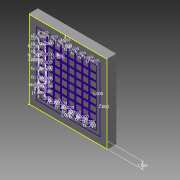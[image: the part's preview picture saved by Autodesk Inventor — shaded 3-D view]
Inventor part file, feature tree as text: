
AUTODESK INVENTOR PART (.ipt)
format: ipt  version: 2015 (Build 190159000, 159)  size: 167,424 bytes
history: native  units: in
note: dims shown in document units (in); Inventor stores cm internally (conversion verified against a paired STEP export)
features: fillet x4, sketch x3, extrude x1
ambient origin geometry x8: Origin, YZ Plane, XZ Plane, XY Plane, X Axis, Y Axis, Z Axis, Center Point
bodies: Solid1 (feature_tree)
feature tree (8):
  extrude  "Extrusion1"  Depth=22.0in
  fillet  "Fillet1"  Radius=2.5in
  fillet  "Fillet2"  Radius=0.125in
  fillet  "Fillet3"  Radius=0.125in
  fillet  "Fillet4"  Radius=0.125in
  sketch  "Sketch2"  dims[d7=0.125in]
  sketch  "Sketch3"  dims[d12=1.9688in d13=1.9688in d14=1.9688in d15=1.9688in d16=1.9688in d17=1.9688in d18=1.9688in d19=1.9688in d20=1.9688in d21=1.9688in d22=1.9688in d23=1.9688in d24=1.9688in d25=1.9688in d26=1.9688in d27=1.9688in d28=1.0in d29=1.0in d30=1.0in d31=1.0in d32=2.0in d33=2.0in d34=2.0in d35=2.0in d36=0.2in d37=0.2in d38=0.2in d39=0.2in d40=0.2in d41=0.2in d42=0.2in d43=0.2in d44=0.2in d45=0.2in d46=0.2in d47=0.2in d48=0.2in d49=0.2in d50=0.2in d51=0.2in d52=0.2in d53=0.2in d54=0.2in d55=0.2in d56=0.2in d57=0.2in d58=0.2in d59=0.2in d60=0.2in d61=0.2in d62=0.2in d63=1.5688in d64=1.5688in d65=0.2in]
  sketch  "Sketch1"  dims[d0=22.0in d1=22.0in d2=2.5in d3=0.0in d4=0.125in d5=0.125in d6=0.125in]
